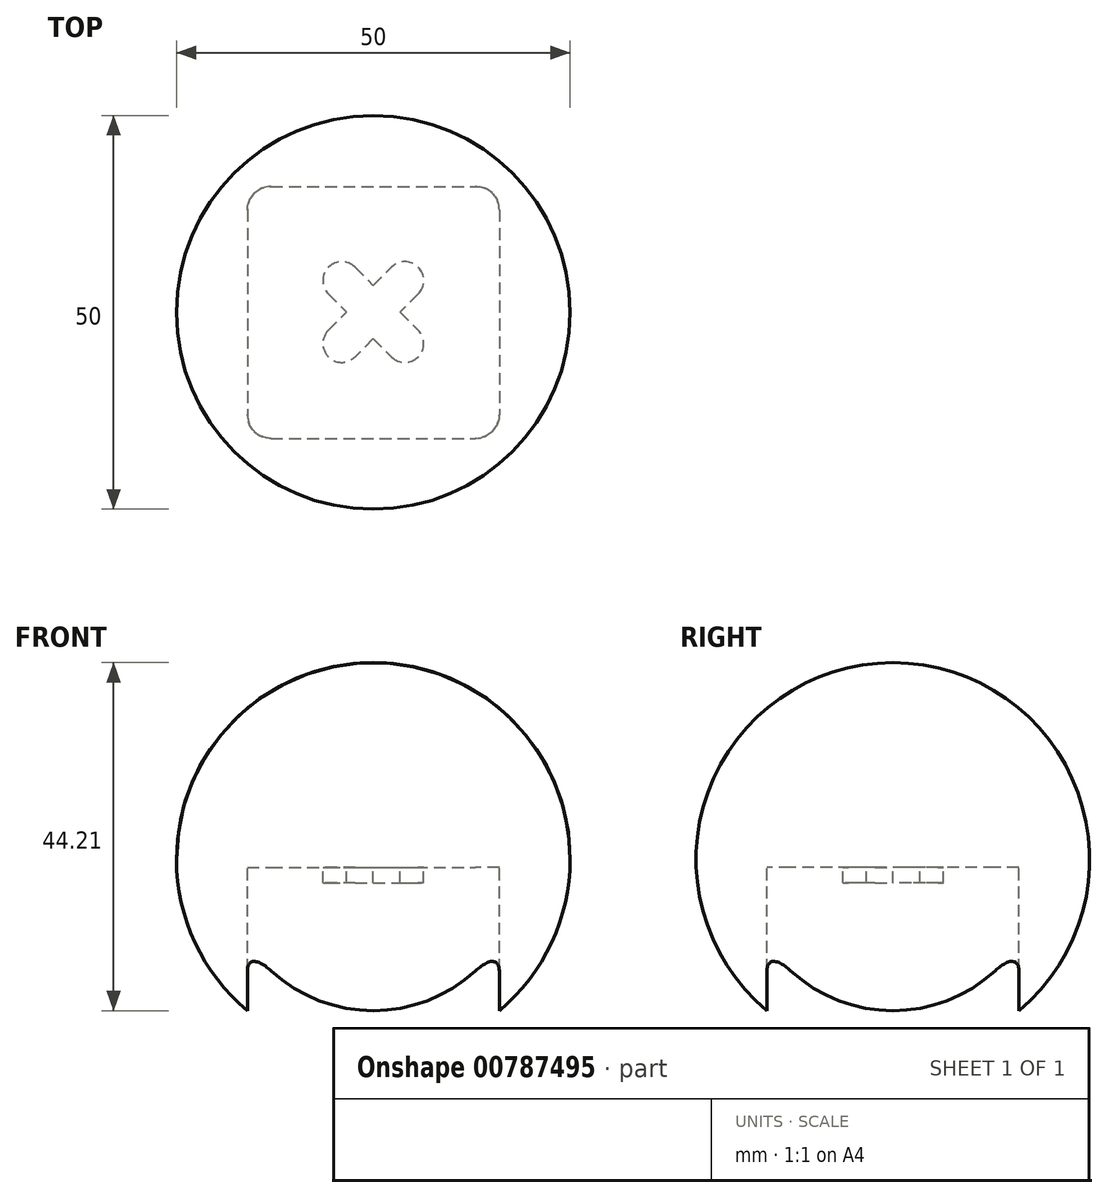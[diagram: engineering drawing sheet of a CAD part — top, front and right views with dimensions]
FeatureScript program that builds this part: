
annotation { "Feature Type Name" : "Feature", "Feature Type Description" : "" }
export const myFeature = defineFeature(function(context is Context, id is Id, definition is map)
    precondition{}
    {
        {
            var Q0;
            Q0=qCreatedBy(makeId("Top.planeOp"),FACE);
            var sketch = newSketch(context, id + "F0", { "sketchPlane" : qUnion([Q0])});
            skArc(sketch, "E0", {"start": v(-2.3, 5.74) * mm, "mid": v(-5.7, 5.74) * mm, "end": v(-5.7, 2.34) * mm});
            skArc(sketch, "E1", {"start": v(5.7, 2.34) * mm, "mid": v(5.7, 5.74) * mm, "end": v(2.3, 5.74) * mm});
            skArc(sketch, "E2", {"start": v(-5.7, -2.26) * mm, "mid": v(-5.7, -5.66) * mm, "end": v(-2.3, -5.66) * mm});
            skArc(sketch, "E3", {"start": v(2.3, -5.66) * mm, "mid": v(5.7, -5.66) * mm, "end": v(5.7, -2.26) * mm});
            skLineSegment(sketch, "E4", {"start": v(-5.7, -2.26) * mm, "end": v(-3.4, 0.04) * mm});
            skLineSegment(sketch, "E5", {"start": v(5.7, 2.34) * mm, "end": v(3.4, 0.04) * mm});
            skLineSegment(sketch, "E6", {"start": v(-2.3, 5.74) * mm, "end": v(0, 3.43) * mm});
            skLineSegment(sketch, "E7", {"start": v(-5.7, 2.34) * mm, "end": v(-3.4, 0.04) * mm});
            skLineSegment(sketch, "E8.trimOffspring", {"start": v(0, 3.43) * mm, "end": v(2.3, 5.74) * mm});
            skLineSegment(sketch, "E9.trimOffspring", {"start": v(3.4, 0.04) * mm, "end": v(5.7, -2.26) * mm});
            skLineSegment(sketch, "E10.trimOffspring", {"start": v(0, -3.36) * mm, "end": v(-2.3, -5.66) * mm});
            skLineSegment(sketch, "E11.trimOffspring", {"start": v(0, -3.36) * mm, "end": v(2.3, -5.66) * mm});
            skSolve(sketch);
        }
        {
            var Q0;
            Q0=makeQuery(id+"F0.imprint","IMPRINT",FACE,{"disambiguationData":[TD([[makeQuery(id+"F0.imprint","IMPRINT",EDGE,{"derivedFrom":sQuery(id+"F0.wireOp",EDGE,"E0")}),1.0]])]});
            extrude(context, id + "F1", {"entities" : qUnion([Q0]), "depth" : 2 * mm, "offsetDistance" : 25 * mm});
        }
        {
            var Q0;
            Q0=qCreatedBy(makeId("Front.planeOp"),FACE);
            var sketch = newSketch(context, id + "F2", { "sketchPlane" : qUnion([Q0])});
            skLineSegment(sketch, "E12", {"start": v(0, 26) * mm, "end": v(0, -24) * mm, "construction": true});
            skPoint(sketch, "E13", {"position": v(0, 1) * mm});
            skLineSegment(sketch, "E14", {"start": v(-22.81, 1) * mm, "end": v(21.9, 1) * mm, "construction": true});
            skArc(sketch, "E15", {"start": v(-25, 1) * mm, "mid": v(0, -24) * mm, "end": v(25, 1) * mm});
            skPoint(sketch, "E16", {"position": v(0, -24) * mm});
            skLineSegment(sketch, "E17", {"start": v(-25, 1) * mm, "end": v(25, 1) * mm});
            skSolve(sketch);
        }
        {
            var Q0;
            Q0=makeQuery(id+"F2.imprint","IMPRINT",FACE,{"disambiguationData":[TD([[makeQuery(id+"F2.imprint","IMPRINT",EDGE,{"derivedFrom":sQuery(id+"F2.wireOp",EDGE,"E15")}),1.0]])]});
            var Q1;
            Q1=sQuery(id+"F2.wireOp",EDGE,"E14");
            revolve(context, id + "F3", {"operationType" : NewBodyOperationType.ADD, "surfaceOperationType" : NewSurfaceOperationType.NEW, "entities" : qUnion([Q0]), "axis" : qUnion([Q1]), "revolveType" : RevolveType.FULL});
        }
        {
            var Q0;
            Q0=qCreatedBy(makeId("Top.planeOp"),FACE);
            var sketch = newSketch(context, id + "F4", { "sketchPlane" : qUnion([Q0])});
            skLineSegment(sketch, "E18.bottom", {"start": v(-13, 16) * mm, "end": v(13, 16) * mm});
            skLineSegment(sketch, "E18.top", {"start": v(-13, -16) * mm, "end": v(13, -16) * mm});
            skLineSegment(sketch, "E18.left", {"start": v(-16, 13) * mm, "end": v(-16, -13) * mm});
            skLineSegment(sketch, "E18.right", {"start": v(16, 13) * mm, "end": v(16, -13) * mm});
            skPoint(sketch, "E19", {"position": v(0, 16) * mm});
            skPoint(sketch, "E20", {"position": v(16, 0) * mm});
            skPoint(sketch, "E21.visualSharp", {"position": v(16, 16) * mm});
            skArc(sketch, "E21.filletArc", {"start": v(16, 13) * mm, "mid": v(15.12, 15.12) * mm, "end": v(13, 16) * mm});
            skPoint(sketch, "E22.visualSharp", {"position": v(16, -16) * mm});
            skArc(sketch, "E22.filletArc", {"start": v(13, -16) * mm, "mid": v(15.12, -15.12) * mm, "end": v(16, -13) * mm});
            skPoint(sketch, "E23.visualSharp", {"position": v(-16, -16) * mm});
            skArc(sketch, "E23.filletArc", {"start": v(-16, -13) * mm, "mid": v(-15.12, -15.12) * mm, "end": v(-13, -16) * mm});
            skPoint(sketch, "E24.visualSharp", {"position": v(-16, 16) * mm});
            skArc(sketch, "E24.filletArc", {"start": v(-13, 16) * mm, "mid": v(-15.12, 15.12) * mm, "end": v(-16, 13) * mm});
            skSolve(sketch);
        }
        {
            var Q0;
            Q0 = qSketchRegion(id + "F4", true);
            extrude(context, id + "F5", {"entities" : qUnion([Q0]), "operationType" : NewBodyOperationType.REMOVE, "oppositeDirection" : true, "depth" : 25 * mm, "offsetDistance" : 25 * mm});
        }
        {
            var Q0;
            Q0=makeQuery(id+"F0.imprint","IMPRINT",FACE,{"disambiguationData":[TD([[makeQuery(id+"F0.imprint","IMPRINT",EDGE,{"derivedFrom":sQuery(id+"F0.wireOp",EDGE,"E0")}),1.0]])]});
            extrude(context, id + "F6", {"entities" : qUnion([Q0]), "operationType" : NewBodyOperationType.ADD, "oppositeDirection" : true, "depth" : 2 * mm, "offsetDistance" : 25 * mm});
        }
    });
